# Revit family: 1194xxx Monza 250 Classic
name_source: partatom
category: Lighting Fixtures
revit_build: Autodesk Revit 2018 (Build: 20170223_1515(x64)
units: mm (PartAtom-declared; Revit-internal decimal feet)

## family parameters
Always vertical = Yes
Cut with Voids When Loaded = No
Host = Wall
Light Source = No
OmniClass Number = 23.80.70.00
OmniClass Title = Lighting
Part Type = Normal
Room Calculation Point = No
Round Connector Dimension = Use Diameter
Shared = No

## types (4) — shared parameters
ADA compliant = N / A
Driver Required = No
Electrical Class = 2
Light Source Fixed = Yes
Location / IP Rating = IP44
Main Material = Metal - Steel
Manufacturer = Astro Lighting Ltd
Manufacturer URL - Europe and Rest of World = www.astrolighting.com
Manufacturer URL - North America = us.astrolighting.com
Product Dimensions (MM) = 250 X 125 X 90
Product Location = Zone 2, 3
Product URL = https://www.astrolighting.com
URL = www.astrolighting.com

## per-type parameters (varying)
| type | Dimmable | Dimming Method | Driver Included | Efficacy (lm/w) | Lamp | Main Finish | Power (Watts) | Product CCT | Product CRI | Product Name | Product SKU | Product Weight (KG) | Wattage Comments |
| CE | No |  | Yes | 40 | LED | Polished Chrome | 4.7 | 3000K | 80 | Monza 250 LED | 1194017 | 1.7 |  |
| Astro Monza 250 Polished Chrome | No |  | Yes | 40 | LED | Polished Chrome | 4.7 | 3000K | 80 | Monza 250 LED | 1194017 | 1.7 |  |
| Astro Monza 250 Bronze | No |  | Yes | 40 | LED | Bronze | 4.7 | 3000K | 80 | Monza 250 LED | 1194019 | 1.7 |  |
| Monza 250 Classic | Yes | Lamp Dependent |  | Lamp Dependent | E27 | Polished Chrome | Lamp Dependent | Lamp Dependent | Lamp Dependent | Monza 250 Classic | 1194003 | 1.334 | 12W Max |

## geometry (parser evidence)
native form markers: Sweep x2
no freeform markers — native parametric forms only
